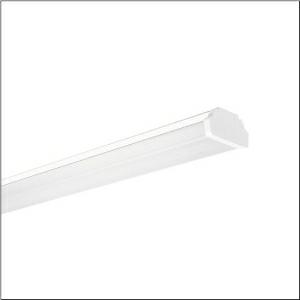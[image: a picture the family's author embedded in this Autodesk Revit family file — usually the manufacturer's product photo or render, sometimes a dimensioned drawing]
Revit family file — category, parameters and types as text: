
# Revit family: dus_r__31_gen_2_53bd812mv4cxd2_64ed
name_source: partatom
category: Lighting Fixtures
units: mm (PartAtom-declared; Revit-internal decimal feet)

## family parameters
Cut with Voids When Loaded = No
Host = Face
Light Source = No
Part Type = Normal
Room Calculation Point = No
Round Connector Dimension = Use Diameter
Shared = No

## types (1)
- --- (1 x LED, 12350 lm, 64.6 W, 4000K)
    Apparent Load = 65 VA
    CIE Flux Codes = 47 80 95 93 100
    Color Rendering = 80
    Color Temperature = 4000K
    Default Elevation = 1800 mm
    Description = DUS® 31 Gen.2, luminaire insert, of sheet steel, coil coated, white, length: 1.535mm, width: 81mm, height: 90mm, 5x system unit, system units: 307mm, LED rated luminous flux: 12.350lm, light colour: 840, control gear: ON/OFF Multilumen, control gear: ECG, with plug, 3-pole, with phase selection, mains connection: 220..240V, AC, 50/60Hz, rated input power: 65W, through-wiring accessed according to module size, primary optical cover: cover, of PMMA, light emission: direct distribution, primary light characteristic: symmetric, protection rating (complete): IP20, protection rating (LED compartment): IP50, insulation class (complete): insulation class I (protective earthing), certification: CE, ENEC, VDE, UKCA, impact resistance: IK03, permissible ambient temperature for indoor applications: -35..+40°C, corresponds to IFS (International Featured Standards) requirements for safety and quality in the food industry, reducing of maximum allowable ambient temperature of 5°C with ceiling mounting, packaging unit: 1 piece
    Height = 95 mm
    Lamp = 1 x LED
    Lamp Light Flux = 12350 lm
    Lamp Power = 64.6 W
    Lamp count = 1
    Length = 1535 mm
    Luminous efficacy = 191 lm/W
    Manufacturer = Siteco
    ModVariant = No
    Model = 53BD812MV4CXD2
    Mounting Place = Ceiling
    Mounting Type = Pendant
    Number of Poles = 1
    OnlyDefault = Yes
    Power Factor = 1
    Product Name = DUS® 31 Gen.2
    Product group = luminaire insert | ceiling pendant
    ProductGroupID = 902
    Protection Class = Protection class I
    Protection Degree = IP 20
    RLX_Detail_Level = 1
    RLX_Emergency_Light_Flux = 0 lm
    RLX_Emergency_Type = 0
    RLX_Emergency_Type_DB = No
    RlxData = <blob elided: 29857 chars, md5=8d6a905e>
    Socket = socket
    Standby Power = 0 W
    System Light Flux = 12350 lm
    System Power = 65 W
    Type Comments = factory setting: luminous flux: 100 % | (A | C | E) | 152 mA
    Type Image = l_1319596.jpg
    URL = http://relux.com
    VarID = @adj_054233
    Voltage = 0 V
    Weight = 0.00 kg
    Width = 81 mm

## geometry (parser evidence)
native form markers: Blend x4, Sweep x14
no freeform markers — native parametric forms only
